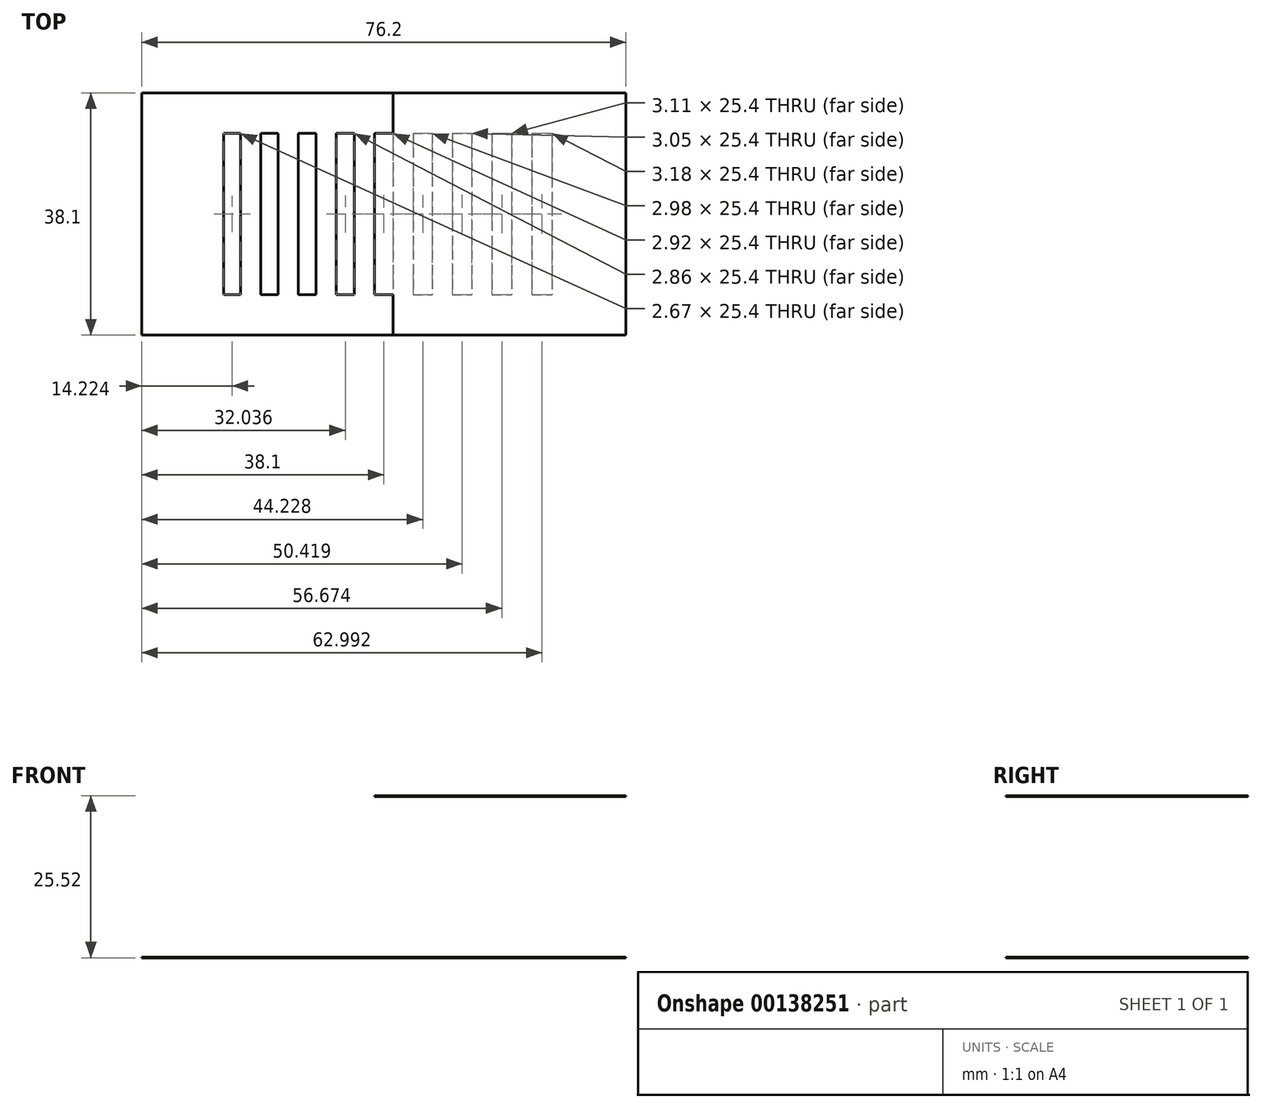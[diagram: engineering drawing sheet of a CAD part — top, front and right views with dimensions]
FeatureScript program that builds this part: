
annotation { "Feature Type Name" : "Feature", "Feature Type Description" : "" }
export const myFeature = defineFeature(function(context is Context, id is Id, definition is map)
    precondition{}
    {
        {
            assignVariable(context, id + "F0", {"name" : "MAT", "anyValue" : .125});
        }
        {
            var Q0;
            Q0=qCreatedBy(makeId("Top.planeOp"),FACE);
            var sketch = newSketch(context, id + "F1", { "sketchPlane" : qUnion([Q0])});
            skLineSegment(sketch, "E0.rect.bottom", {"start": v(-38.1, 19.05) * mm, "end": v(38.1, 19.05) * mm});
            skLineSegment(sketch, "E0.rect.top", {"start": v(-38.1, -19.05) * mm, "end": v(38.1, -19.05) * mm});
            skLineSegment(sketch, "E0.rect.left", {"start": v(-38.1, 19.05) * mm, "end": v(-38.1, -19.05) * mm});
            skLineSegment(sketch, "E0.rect.right", {"start": v(38.1, 19.05) * mm, "end": v(38.1, -19.05) * mm});
            skPoint(sketch, "E0.rect.middle", {"position": v(0, 0) * mm});
            skLineSegment(sketch, "E1.bottom", {"start": v(-25.2, 12.7) * mm, "end": v(-22.54, 12.7) * mm});
            skLineSegment(sketch, "E1.top", {"start": v(-25.2, -12.7) * mm, "end": v(-22.54, -12.7) * mm});
            skLineSegment(sketch, "E1.left", {"start": v(-25.2, 12.7) * mm, "end": v(-25.2, -12.7) * mm});
            skLineSegment(sketch, "E1.right", {"start": v(-22.54, 12.7) * mm, "end": v(-22.54, -12.7) * mm});
            skLineSegment(sketch, "E2.bottom", {"start": v(-7.5, 12.7) * mm, "end": v(-4.64, 12.7) * mm});
            skLineSegment(sketch, "E2.top", {"start": v(-7.5, -12.7) * mm, "end": v(-4.64, -12.7) * mm});
            skLineSegment(sketch, "E2.left", {"start": v(-7.5, 12.7) * mm, "end": v(-7.5, -12.7) * mm});
            skLineSegment(sketch, "E2.right", {"start": v(-4.64, 12.7) * mm, "end": v(-4.64, -12.7) * mm});
            skLineSegment(sketch, "E3.bottom", {"start": v(-1.46, 12.7) * mm, "end": v(1.46, 12.7) * mm});
            skLineSegment(sketch, "E3.top", {"start": v(-1.46, -12.7) * mm, "end": v(1.46, -12.7) * mm});
            skLineSegment(sketch, "E3.left", {"start": v(-1.46, 12.7) * mm, "end": v(-1.46, -12.7) * mm});
            skLineSegment(sketch, "E3.right", {"start": v(1.46, 12.7) * mm, "end": v(1.46, -12.7) * mm});
            skLineSegment(sketch, "E4.bottom", {"start": v(4.64, 12.7) * mm, "end": v(7.62, 12.7) * mm});
            skLineSegment(sketch, "E4.top", {"start": v(4.64, -12.7) * mm, "end": v(7.62, -12.7) * mm});
            skLineSegment(sketch, "E4.left", {"start": v(4.64, 12.7) * mm, "end": v(4.64, -12.7) * mm});
            skLineSegment(sketch, "E4.right", {"start": v(7.62, 12.7) * mm, "end": v(7.62, -12.7) * mm});
            skLineSegment(sketch, "E5.bottom", {"start": v(23.3, 12.7) * mm, "end": v(26.48, 12.7) * mm});
            skLineSegment(sketch, "E5.top", {"start": v(23.3, -12.7) * mm, "end": v(26.48, -12.7) * mm});
            skLineSegment(sketch, "E5.left", {"start": v(23.3, 12.7) * mm, "end": v(23.3, -12.7) * mm});
            skLineSegment(sketch, "E5.right", {"start": v(26.48, 12.7) * mm, "end": v(26.48, -12.7) * mm});
            skPoint(sketch, "E6", {"position": v(0, 12.7) * mm});
            skLineSegment(sketch, "E7.bottom", {"start": v(10.8, 12.7) * mm, "end": v(13.84, 12.7) * mm});
            skLineSegment(sketch, "E7.top", {"start": v(10.8, -12.7) * mm, "end": v(13.84, -12.7) * mm});
            skLineSegment(sketch, "E7.left", {"start": v(10.8, 12.7) * mm, "end": v(10.8, -12.7) * mm});
            skLineSegment(sketch, "E7.right", {"start": v(13.84, 12.7) * mm, "end": v(13.84, -12.7) * mm});
            skLineSegment(sketch, "E8.bottom", {"start": v(17.02, 12.7) * mm, "end": v(20.13, 12.7) * mm});
            skLineSegment(sketch, "E8.top", {"start": v(17.02, -12.7) * mm, "end": v(20.13, -12.7) * mm});
            skLineSegment(sketch, "E8.left", {"start": v(17.02, 12.7) * mm, "end": v(17.02, -12.7) * mm});
            skLineSegment(sketch, "E8.right", {"start": v(20.13, 12.7) * mm, "end": v(20.13, -12.7) * mm});
            skLineSegment(sketch, "E9.bottom", {"start": v(-10.67, 12.7) * mm, "end": v(-13.46, 12.7) * mm});
            skLineSegment(sketch, "E9.top", {"start": v(-10.67, -12.7) * mm, "end": v(-13.46, -12.7) * mm});
            skLineSegment(sketch, "E9.left", {"start": v(-10.67, 12.7) * mm, "end": v(-10.67, -12.7) * mm});
            skLineSegment(sketch, "E9.right", {"start": v(-13.46, 12.7) * mm, "end": v(-13.46, -12.7) * mm});
            skLineSegment(sketch, "E10.bottom", {"start": v(-16.64, 12.7) * mm, "end": v(-19.37, 12.7) * mm});
            skLineSegment(sketch, "E10.top", {"start": v(-16.64, -12.7) * mm, "end": v(-19.37, -12.7) * mm});
            skLineSegment(sketch, "E10.left", {"start": v(-16.64, 12.7) * mm, "end": v(-16.64, -12.7) * mm});
            skLineSegment(sketch, "E10.right", {"start": v(-19.37, 12.7) * mm, "end": v(-19.37, -12.7) * mm});
            skSolve(sketch);
        }
        {
            var Q0;
            Q0=qSketchRegion(id+"F1",true);
            extrude(context, id + "F2", {"entities" : qUnion([Q0]), "depth" : (getVariable(context, 'MAT')) * mm});
        }
        {
            var Q0;
            Q0=qCreatedBy(makeId("Top.planeOp"),FACE);
            cPlane(context, id + "F3", {"entities" : qUnion([Q0]), "cplaneType" : CPlaneType.OFFSET, "offset" : 25.4 * mm, "width" : 152.4 * mm, "height" : 152.4 * mm});
        }
        {
            var Q0;
            Q0=qCreatedBy(id+"F3.planeOp",FACE);
            var sketch = newSketch(context, id + "F4", { "sketchPlane" : qUnion([Q0])});
            skLineSegment(sketch, "E11.0", {"start": v(-1.46, 12.7) * mm, "end": v(1.46, 12.7) * mm});
            skLineSegment(sketch, "E12.0", {"start": v(-1.46, -12.7) * mm, "end": v(1.46, -12.7) * mm});
            skLineSegment(sketch, "E13.0", {"start": v(-1.46, 12.7) * mm, "end": v(-1.46, -12.7) * mm});
            skLineSegment(sketch, "E14.0", {"start": v(-38.1, 19.05) * mm, "end": v(38.1, 19.05) * mm});
            skLineSegment(sketch, "E15.0", {"start": v(-38.1, -19.05) * mm, "end": v(38.1, -19.05) * mm});
            skLineSegment(sketch, "E16", {"start": v(1.46, 12.7) * mm, "end": v(1.46, 19.05) * mm});
            skLineSegment(sketch, "E17", {"start": v(1.46, -12.7) * mm, "end": v(1.46, -19.05) * mm});
            skLineSegment(sketch, "E18.0", {"start": v(38.1, 19.05) * mm, "end": v(38.1, -19.05) * mm});
            skSolve(sketch);
        }
        {
            var Q0;
            Q0=qSketchRegion(id+"F4",true);
            extrude(context, id + "F5", {"entities" : qUnion([Q0]), "depth" : (getVariable(context, 'MAT')) * mm});
        }
    });
